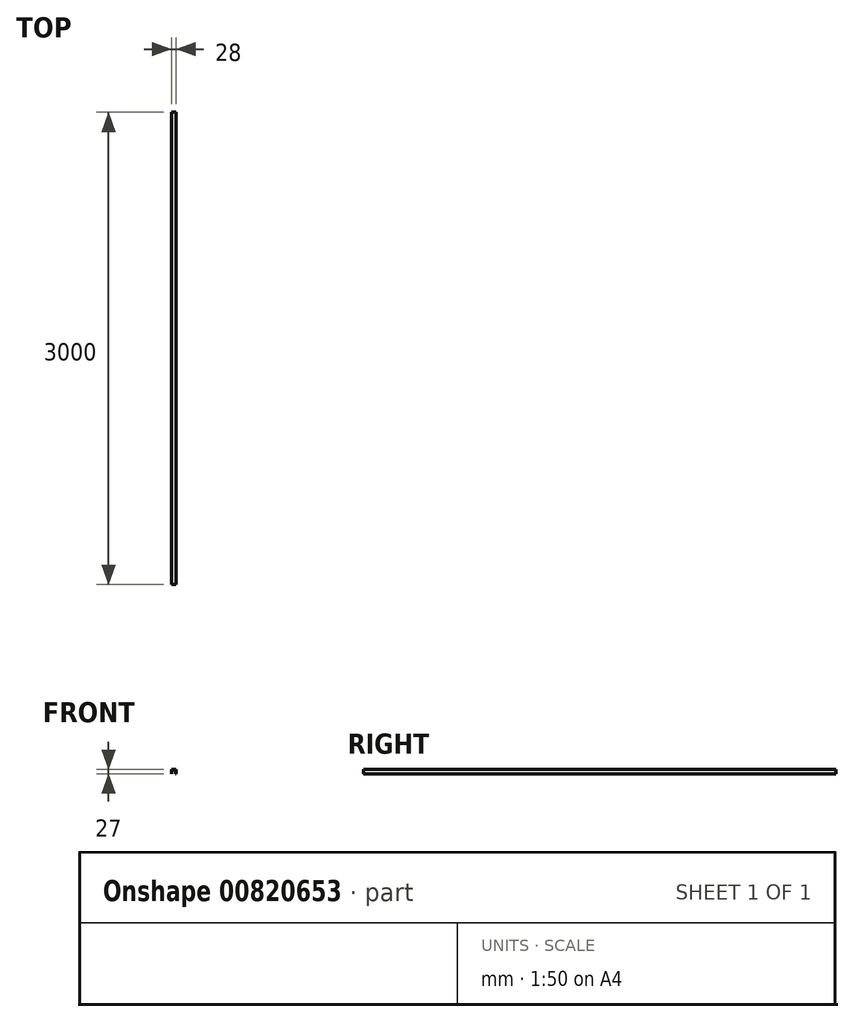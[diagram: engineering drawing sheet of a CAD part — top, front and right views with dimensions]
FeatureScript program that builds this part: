
annotation { "Feature Type Name" : "Feature", "Feature Type Description" : "" }
export const myFeature = defineFeature(function(context is Context, id is Id, definition is map)
    precondition{}
    {
        {
            var Q0;
            Q0=qCreatedBy(makeId("Front.planeOp"),FACE);
            var sketch = newSketch(context, id + "F0", { "sketchPlane" : qUnion([Q0])});
            skLineSegment(sketch, "E0.bottom", {"start": v(14, 13.5) * mm, "end": v(-14, 13.5) * mm});
            skLineSegment(sketch, "E0.top", {"start": v(14, -13.5) * mm, "end": v(13, -13.5) * mm});
            skLineSegment(sketch, "E0.left", {"start": v(14, 13.5) * mm, "end": v(14, -13.5) * mm});
            skLineSegment(sketch, "E0.right", {"start": v(-14, 13.5) * mm, "end": v(-14, -13.5) * mm});
            skPoint(sketch, "E0.middle", {"position": v(0, 0) * mm});
            skLineSegment(sketch, "E1", {"start": v(-13, -13.5) * mm, "end": v(-13, 12.5) * mm});
            skLineSegment(sketch, "E2", {"start": v(-13, 12.5) * mm, "end": v(13, 12.5) * mm});
            skLineSegment(sketch, "E3", {"start": v(13, 12.5) * mm, "end": v(13, -13.5) * mm});
            skLineSegment(sketch, "E4.trimOffspring", {"start": v(-13, -13.5) * mm, "end": v(-14, -13.5) * mm});
            skSolve(sketch);
        }
        {
            var Q0;
            Q0=makeQuery(id+"F0.imprint","IMPRINT",FACE,{"disambiguationData":[TD([[makeQuery(id+"F0.imprint","IMPRINT",EDGE,{"derivedFrom":sQuery(id+"F0.wireOp",EDGE,"E0.bottom")}),1.0]])]});
            extrude(context, id + "F1", {"entities" : qUnion([Q0]), "endBound" : BoundingType.SYMMETRIC, "depth" : 3000 * mm, "offsetDistance" : 25 * mm});
        }
    });
